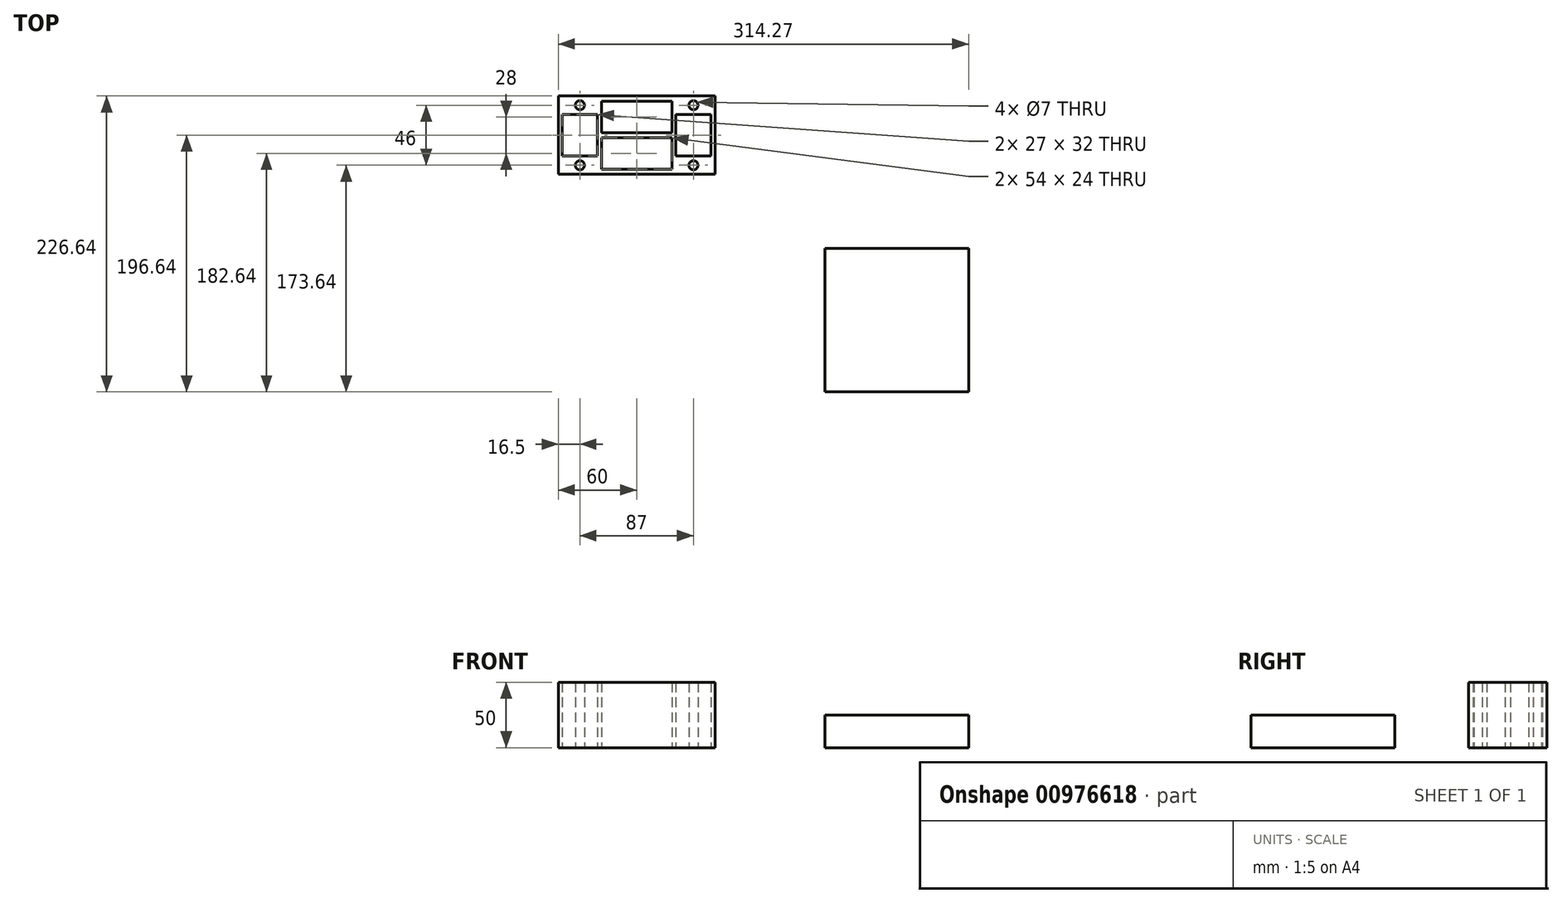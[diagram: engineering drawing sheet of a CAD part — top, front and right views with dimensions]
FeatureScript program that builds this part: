
annotation { "Feature Type Name" : "Feature", "Feature Type Description" : "" }
export const myFeature = defineFeature(function(context is Context, id is Id, definition is map)
    precondition{}
    {
        {
            var Q0;
            Q0=qCreatedBy(makeId("Top.planeOp"),FACE);
            var sketch = newSketch(context, id + "F0", { "sketchPlane" : qUnion([Q0])});
            skLineSegment(sketch, "E0.bottom", {"start": v(60, 30) * mm, "end": v(-60, 30) * mm});
            skLineSegment(sketch, "E0.top", {"start": v(60, -30) * mm, "end": v(-60, -30) * mm});
            skLineSegment(sketch, "E0.left", {"start": v(60, 30) * mm, "end": v(60, -30) * mm});
            skLineSegment(sketch, "E0.right", {"start": v(-60, 30) * mm, "end": v(-60, -30) * mm});
            skPoint(sketch, "E0.middle", {"position": v(0, 0) * mm});
            skLineSegment(sketch, "E1.bottom", {"start": v(60, 30) * mm, "end": v(27, 30) * mm});
            skLineSegment(sketch, "E1.top", {"start": v(60, -30) * mm, "end": v(27, -30) * mm});
            skLineSegment(sketch, "E1.right", {"start": v(27, 26) * mm, "end": v(27, 2) * mm});
            skLineSegment(sketch, "E2.bottom", {"start": v(-60, 30) * mm, "end": v(-27, 30) * mm});
            skLineSegment(sketch, "E2.top", {"start": v(-60, -30) * mm, "end": v(-27, -30) * mm});
            skLineSegment(sketch, "E2.right", {"start": v(-27, 26) * mm, "end": v(-27, 2) * mm});
            skCircle(sketch, "E3", {"center": v(-43.5, 23) * mm, "radius": 3.5 * mm});
            skCircle(sketch, "E4", {"center": v(-43.5, -23) * mm, "radius": 3.5 * mm});
            skCircle(sketch, "E5", {"center": v(43.5, 23) * mm, "radius": 3.5 * mm});
            skCircle(sketch, "E6", {"center": v(43.5, -23) * mm, "radius": 3.5 * mm});
            skLineSegment(sketch, "E7.bottom", {"start": v(22.5, 26) * mm, "end": v(-22.5, 26) * mm});
            skLineSegment(sketch, "E7.top", {"start": v(22.5, -26) * mm, "end": v(-22.5, -26) * mm});
            skLineSegment(sketch, "E8", {"start": v(-43.5, -19.5) * mm, "end": v(-43.5, -16) * mm});
            skLineSegment(sketch, "E9.bottom", {"start": v(-43.5, -16) * mm, "end": v(-43.5, -16) * mm});
            skLineSegment(sketch, "E9.top", {"start": v(-43.5, 48) * mm, "end": v(-43.5, 48) * mm});
            skLineSegment(sketch, "E9.right", {"start": v(-43.5, 26.5) * mm, "end": v(-43.5, 48) * mm});
            skPoint(sketch, "E9.middle", {"position": v(-43.5, 16) * mm});
            skLineSegment(sketch, "E10.bottom", {"start": v(-30, 16) * mm, "end": v(-57, 16) * mm});
            skLineSegment(sketch, "E10.top", {"start": v(-30, -16) * mm, "end": v(-57, -16) * mm});
            skLineSegment(sketch, "E10.left", {"start": v(-30, 16) * mm, "end": v(-30, -16) * mm});
            skLineSegment(sketch, "E10.right", {"start": v(-57, 16) * mm, "end": v(-57, -16) * mm});
            skPoint(sketch, "E10.middle", {"position": v(-43.5, 0) * mm});
            skLineSegment(sketch, "E11.bottom", {"start": v(57, 16) * mm, "end": v(30, 16) * mm});
            skLineSegment(sketch, "E11.top", {"start": v(57, -16) * mm, "end": v(30, -16) * mm});
            skLineSegment(sketch, "E11.left", {"start": v(57, 16) * mm, "end": v(57, -16) * mm});
            skLineSegment(sketch, "E11.right", {"start": v(30, 16) * mm, "end": v(30, -16) * mm});
            skPoint(sketch, "E11.middle", {"position": v(43.5, 0) * mm});
            skLineSegment(sketch, "E12", {"start": v(-22.5, 26) * mm, "end": v(-27, 26) * mm});
            skLineSegment(sketch, "E13", {"start": v(22.5, 26) * mm, "end": v(27, 26) * mm});
            skLineSegment(sketch, "E14", {"start": v(22.5, -26) * mm, "end": v(27, -26) * mm});
            skLineSegment(sketch, "E15", {"start": v(-22.5, -26) * mm, "end": v(-27, -26) * mm});
            skPoint(sketch, "E16.start.orphan", {"position": v(-60, 0) * mm});
            skPoint(sketch, "E17.trimOffspring.end.orphan", {"position": v(-27, 0) * mm});
            skPoint(sketch, "E18.trimOffspring.start.orphan", {"position": v(27, 0) * mm});
            skPoint(sketch, "E19.start.orphan", {"position": v(43.5, 30) * mm});
            skPoint(sketch, "E20.orphan", {"position": v(43.5, 16) * mm});
            skPoint(sketch, "E21.trimOffspring.end.orphan", {"position": v(60, 0) * mm});
            skPoint(sketch, "E22.start.orphan", {"position": v(43.5, -30) * mm});
            skPoint(sketch, "E23.orphan", {"position": v(-43.5, -30) * mm});
            skPoint(sketch, "E24.start.orphan", {"position": v(-43.5, 30) * mm});
            skLineSegment(sketch, "E25.bottom", {"start": v(27, 2) * mm, "end": v(-27, 2) * mm});
            skLineSegment(sketch, "E25.top", {"start": v(27, -2) * mm, "end": v(-27, -2) * mm});
            skLineSegment(sketch, "E26.trimOffspring", {"start": v(27, -2) * mm, "end": v(27, -26) * mm});
            skLineSegment(sketch, "E27", {"start": v(-27, -2) * mm, "end": v(-27, -26) * mm});
            skSolve(sketch);
        }
        {
            var Q0;
            Q0 = qSketchRegion(id + "F0", true);
            extrude(context, id + "F1", {"entities" : qUnion([Q0]), "depth" : 50 * mm, "offsetDistance" : 25 * mm});
        }
        {
            var Q0;
            Q0=qCreatedBy(makeId("Top.planeOp"),FACE);
            var sketch = newSketch(context, id + "F2", { "sketchPlane" : qUnion([Q0])});
            skLineSegment(sketch, "E28.bottom", {"start": v(144.27, -196.64) * mm, "end": v(254.27, -196.64) * mm});
            skLineSegment(sketch, "E28.top", {"start": v(144.27, -86.64) * mm, "end": v(254.27, -86.64) * mm});
            skLineSegment(sketch, "E28.left", {"start": v(144.27, -196.64) * mm, "end": v(144.27, -86.64) * mm});
            skLineSegment(sketch, "E28.right", {"start": v(254.27, -196.64) * mm, "end": v(254.27, -86.64) * mm});
            skSolve(sketch);
        }
        {
            var Q0;
            Q0=makeQuery(id+"F2.imprint","IMPRINT",FACE,{"disambiguationData":[TD([[makeQuery(id+"F2.imprint","IMPRINT",EDGE,{"derivedFrom":sQuery(id+"F2.wireOp",EDGE,"E28.bottom")}),1.0]])]});
            extrude(context, id + "F3", {"entities" : qUnion([Q0]), "depth" : 25 * mm, "offsetDistance" : 25 * mm});
        }
    });
